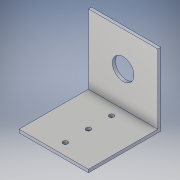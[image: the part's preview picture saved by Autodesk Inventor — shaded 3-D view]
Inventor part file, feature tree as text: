
AUTODESK INVENTOR PART (.ipt)
format: ipt  version: 2019 (Build 230136000, 136)  size: 143,872 bytes
history: native  units: mm
features: sketch x6, extrude x3, hole x2, other x1
ambient origin geometry x8: Origin, YZ Plane, XZ Plane, XY Plane, X Axis, Y Axis, Z Axis, Center Point
bodies: Body1 (feature_tree)
feature tree (12):
  other  "ソリッド1"
  sketch  "スケッチ1"
  sketch  "スケッチ2"
  extrude  "押し出し1"  Depth=45.0mm
  hole  "穴1"  [1 undecoded]
  extrude  "押し出し2"  Depth=2.0mm TaperAngle=0.0deg
  extrude  "押し出し3"  Depth=8.0mm
  hole  "穴2"  [1 undecoded]
  sketch  "スケッチ3"
  sketch  "スケッチ4"
  sketch  "スケッチ5"
  sketch  "スケッチ6"
note: 2 required parameter values undecoded (feature->parameter linkage not recoverable at this tier; creation-order binding heuristic only, values carry confidence <= 0.55)
